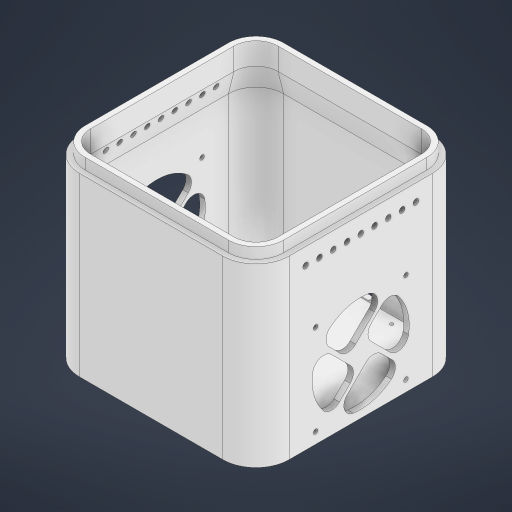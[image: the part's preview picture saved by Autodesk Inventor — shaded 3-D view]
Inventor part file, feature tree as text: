
AUTODESK INVENTOR PART (.ipt)
format: ipt  version: 2024.1 (Build 281209000, 209)  size: 1,241,088 bytes
history: native  units: mm
features: extrude x13, sketch x9, chamfer x4, projected_geometry x4, fillet x3, other x2
ambient origin geometry x8: Origin, YZ Plane, XZ Plane, XY Plane, X Axis, Y Axis, Z Axis, Center Point
bodies: Body1 (feature_tree)
feature tree (35):
  other  "솔리드1"
  sketch  "스케치1"
  extrude  "돌출1"  Depth=190.0mm
  extrude  "돌출2"  Depth=190.0mm
  sketch  "스케치2"
  extrude  "돌출3"  Depth=30.0mm
  extrude  "돌출4"  Depth=5.0mm
  chamfer  "모따기1"  Distance=160.0mm
  extrude  "돌출5"  Depth=5.0mm TaperAngle=0.0deg
  sketch  "스케치5"
  extrude  "돌출6"  Depth=5.0mm
  extrude  "돌출7"  Depth=10.0mm TaperAngle=0.0deg
  extrude  "돌출8"  Depth=10.0mm TaperAngle=0.0deg
  extrude  "돌출9"  Depth=5.0mm TaperAngle=45.0deg
  sketch  "스케치9"
  extrude  "돌출11"  Depth=30.0mm
  extrude  "돌출12"  Depth=33.5mm
  extrude  "돌출13"  Depth=3.0mm
  chamfer  "모따기2"  Distance=6.0mm
  fillet  "모깎기1"  Radius=50.0mm
  fillet  "모깎기2"  Radius=50.0mm
  chamfer  "모따기3"  Distance=3.3mm
  chamfer  "모따기4"  Distance=3.3mm
  extrude  "돌출14"  Depth=15.1mm
  fillet  "모깎기3"  Radius=35.9mm
  projected_geometry  "투영된 루프1"
  sketch  "스케치4"
  sketch  "스케치6"
  sketch  "스케치7"
  projected_geometry  "투영된 루프2"
  sketch  "스케치10"
  projected_geometry  "투영된 루프3"
  sketch  "스케치11"
  projected_geometry  "투영된 루프4"
  other  "Finish1"
